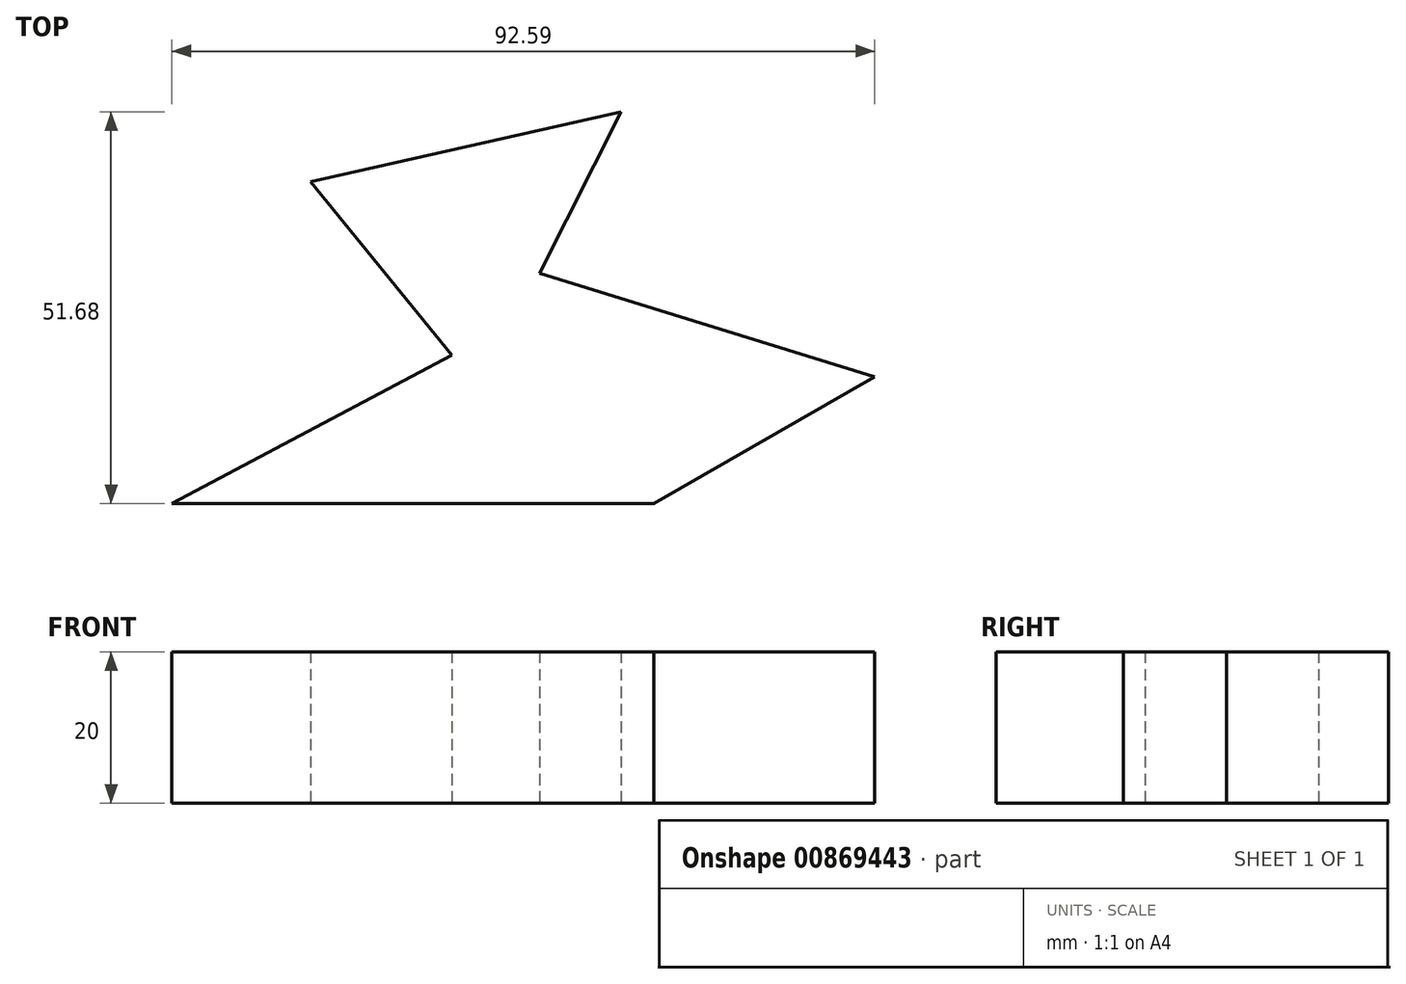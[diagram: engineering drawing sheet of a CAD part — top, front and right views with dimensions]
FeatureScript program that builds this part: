
annotation { "Feature Type Name" : "Feature", "Feature Type Description" : "" }
export const myFeature = defineFeature(function(context is Context, id is Id, definition is map)
    precondition{}
    {
        {
            var Q0;
            Q0=qCreatedBy(makeId("Top.planeOp"),FACE);
            var sketch = newSketch(context, id + "F0", { "sketchPlane" : qUnion([Q0])});
            skLineSegment(sketch, "E0", {"start": v(-63.49, 0) * mm, "end": v(0, 0) * mm});
            skLineSegment(sketch, "E1", {"start": v(0, 0) * mm, "end": v(29.1, 16.71) * mm});
            skLineSegment(sketch, "E2", {"start": v(29.1, 16.71) * mm, "end": v(-15.08, 30.35) * mm});
            skLineSegment(sketch, "E3", {"start": v(-15.08, 30.35) * mm, "end": v(-4.32, 51.68) * mm});
            skLineSegment(sketch, "E4", {"start": v(-4.32, 51.68) * mm, "end": v(-45.24, 42.45) * mm});
            skLineSegment(sketch, "E5", {"start": v(-45.24, 42.45) * mm, "end": v(-26.6, 19.6) * mm});
            skLineSegment(sketch, "E6", {"start": v(-26.6, 19.6) * mm, "end": v(-63.49, 0) * mm});
            skSolve(sketch);
        }
        {
            var Q0;
            Q0=makeQuery(id+"F0.imprint","IMPRINT",FACE,{"disambiguationData":[TD([[makeQuery(id+"F0.imprint","IMPRINT",EDGE,{"derivedFrom":sQuery(id+"F0.wireOp",EDGE,"E0")}),1.0]])]});
            extrude(context, id + "F1", {"entities" : qUnion([Q0]), "depth" : 20 * mm, "offsetDistance" : 25.4 * mm});
        }
        {
            var Q0;
            Q0=makeQuery(id+"F1.opExtrude","CAP_FACE",FACE,{"disambiguationData":[OSD([sQuery(id+"F0.wireOp",EDGE,"E0"),sQuery(id+"F0.wireOp",EDGE,"E1"),sQuery(id+"F0.wireOp",EDGE,"E2"),sQuery(id+"F0.wireOp",EDGE,"E3"),sQuery(id+"F0.wireOp",EDGE,"E4"),sQuery(id+"F0.wireOp",EDGE,"E5"),sQuery(id+"F0.wireOp",EDGE,"E6")])],"isStart":false});
            var sketch = newSketch(context, id + "F2", { "sketchPlane" : qUnion([Q0])});
            skLineSegment(sketch, "E7", {"start": v(-26.6, 19.6) * mm, "end": v(-15.08, 30.35) * mm});
            skSolve(sketch);
        }
    });
